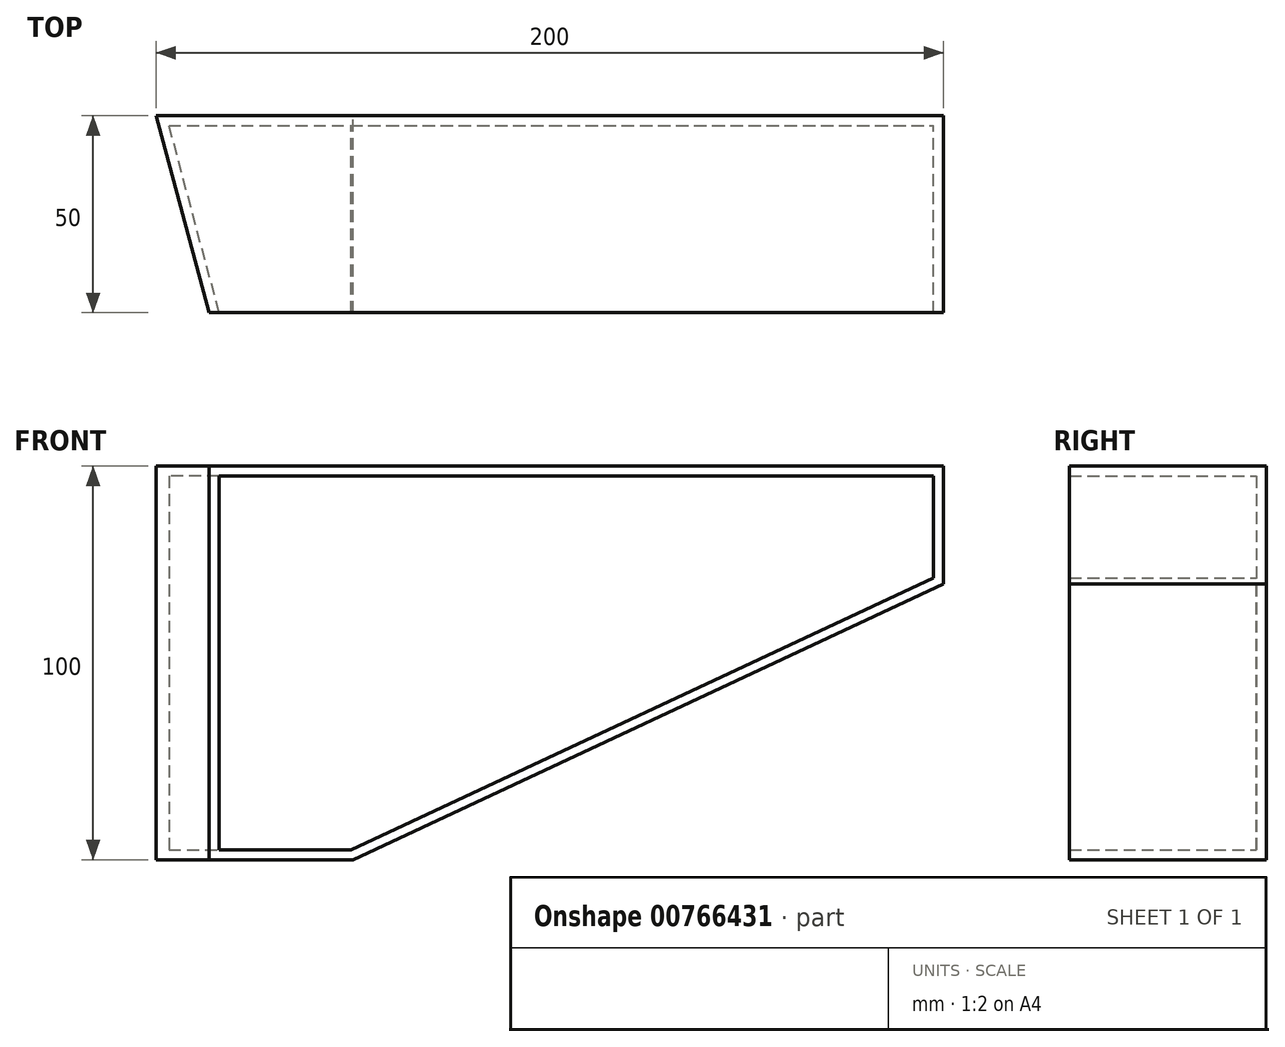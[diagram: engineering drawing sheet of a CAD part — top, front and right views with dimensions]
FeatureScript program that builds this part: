
annotation { "Feature Type Name" : "Feature", "Feature Type Description" : "" }
export const myFeature = defineFeature(function(context is Context, id is Id, definition is map)
    precondition{}
    {
        {
            var Q0;
            Q0=qCreatedBy(makeId("Front.planeOp"),FACE);
            var sketch = newSketch(context, id + "F0", { "sketchPlane" : qUnion([Q0])});
            skLineSegment(sketch, "E0.bottom", {"start": v(-100, 51.43) * mm, "end": v(100, 51.43) * mm});
            skLineSegment(sketch, "E0.top", {"start": v(-100, -48.57) * mm, "end": v(-50, -48.57) * mm});
            skLineSegment(sketch, "E0.right", {"start": v(100, 51.43) * mm, "end": v(100, 21.43) * mm});
            skPoint(sketch, "E1", {"position": v(100, 21.43) * mm});
            skPoint(sketch, "E2", {"position": v(-50, -48.57) * mm});
            skLineSegment(sketch, "E3", {"start": v(-50, -48.57) * mm, "end": v(100, 21.43) * mm});
            skLineSegment(sketch, "E4", {"start": v(-100, 51.43) * mm, "end": v(-100, -48.57) * mm});
            skSolve(sketch);
        }
        {
            var Q0;
            Q0=makeQuery(id+"F0.imprint","IMPRINT",FACE,{"disambiguationData":[TD([[makeQuery(id+"F0.imprint","IMPRINT",EDGE,{"derivedFrom":sQuery(id+"F0.wireOp",EDGE,"E0.bottom")}),-1.0]])]});
            var Q1;
            Q1=sQuery(id+"F0.wireOp",EDGE,"E0.top");
            var Q2;
            Q2=sQuery(id+"F0.wireOp",EDGE,"E0.right");
            var Q3;
            Q3=sQuery(id+"F0.wireOp",EDGE,"E0.bottom");
            var Q4;
            Q4=sQuery(id+"F0.wireOp",EDGE,"E4");
            var Q5;
            Q5=sQuery(id+"F0.wireOp",EDGE,"E3");
            extrude(context, id + "F1", {"entities" : qUnion([Q0]), "surfaceEntities" : qUnion([Q1, Q2, Q3, Q4, Q5]), "depth" : 50 * mm, "offsetDistance" : 25 * mm});
        }
        {
            var Q0;
            Q0=makeQuery(id+"F1.opExtrude","SWEPT_FACE",FACE,{"disambiguationData":[OSD([sQuery(id+"F0.wireOp",EDGE,"E0.bottom")])]});
            var sketch = newSketch(context, id + "F2", { "sketchPlane" : qUnion([Q0])});
            skLineSegment(sketch, "E5", {"start": v(-68.46, -117.72) * mm, "end": v(-100, 0) * mm});
            skLineSegment(sketch, "E6", {"start": v(-100, 0) * mm, "end": v(-122.38, 0) * mm});
            skLineSegment(sketch, "E7", {"start": v(-122.38, 0) * mm, "end": v(-121.38, -70.33) * mm});
            skLineSegment(sketch, "E8", {"start": v(-121.38, -70.33) * mm, "end": v(-68.46, -117.72) * mm});
            skSolve(sketch);
        }
        {
            var Q0;
            Q0=makeQuery(id+"F2.imprint","IMPRINT",FACE,{"disambiguationData":[TD([[makeQuery(id+"F2.imprint","IMPRINT",EDGE,{"derivedFrom":sQuery(id+"F2.wireOp",EDGE,"E6")}),1.0]])]});
            var Q1;
            {var subQ1=sQuery(id+"F0.wireOp",EDGE,"E0.bottom");var subQ2=makeQuery(id+"F1.opExtrude","SWEPT_EDGE",EDGE,{"disambiguationData":[OSD([subQ1,sQuery(id+"F0.wireOp",EDGE,"E4")])]});Q1=makeQuery(id+"F2.imprint","IMPRINT",FACE,{"disambiguationData":[TD([[makeQuery(id+"F2.imprint","IMPRINT",EDGE,{"derivedFrom":subQ2}),-1.0]])]});}
            extrude(context, id + "F3", {"entities" : qUnion([Q0, Q1]), "operationType" : NewBodyOperationType.REMOVE, "endBound" : BoundingType.THROUGH_ALL, "oppositeDirection" : true, "depth" : 25 * mm, "offsetDistance" : 25 * mm});
        }
        {
            var Q0;
            Q0=makeQuery(id+"F1.opExtrude","CAP_FACE",FACE,{"disambiguationData":[OSD([sQuery(id+"F0.wireOp",EDGE,"E0.bottom"),sQuery(id+"F0.wireOp",EDGE,"E0.top"),sQuery(id+"F0.wireOp",EDGE,"E0.right"),sQuery(id+"F0.wireOp",EDGE,"E3"),sQuery(id+"F0.wireOp",EDGE,"E4")])],"isStart":false});
            shell(context, id + "F4", {"entities" : qUnion([Q0]), "thickness" : 2.5 * mm});
        }
    });
